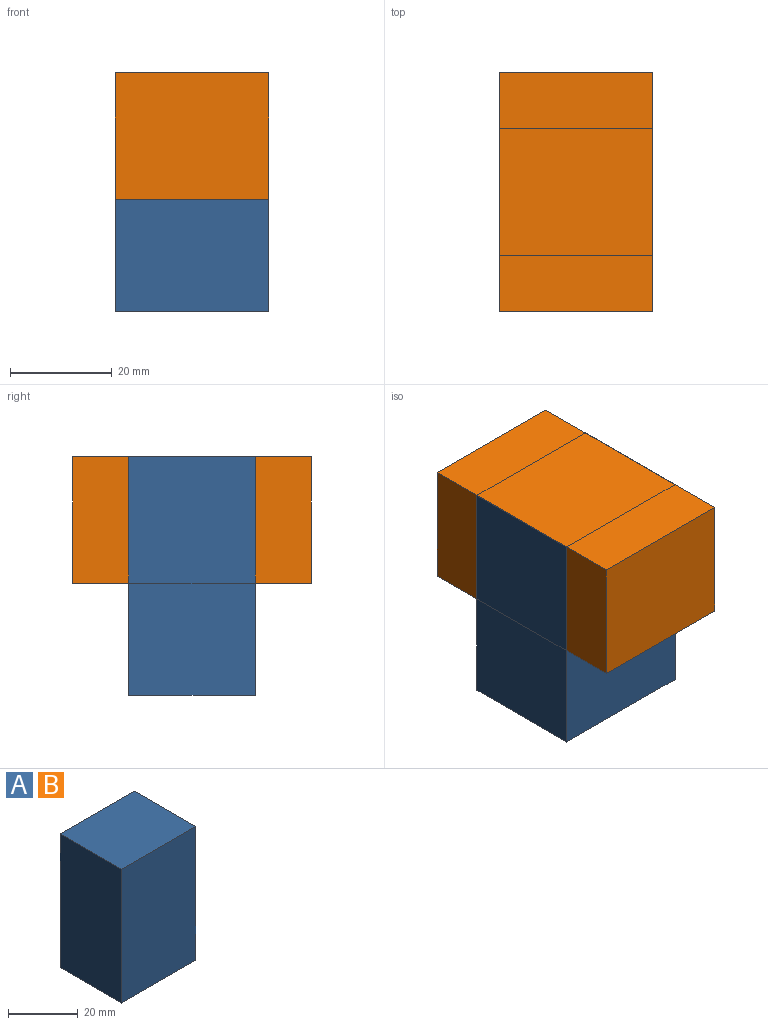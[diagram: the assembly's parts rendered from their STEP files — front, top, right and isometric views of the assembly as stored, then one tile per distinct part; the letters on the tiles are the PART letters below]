
ASSEMBLY  parts=2 mates=1
PART A: 6 faces, bbox 30.2x25x47 mm
  f0: plane 30.18x25mm, normal (0,0,1), area 754.5mm2, adj f1,f3,f4,f5
  f1: plane 47.01x25mm, normal (-1,0,0), area 1175.3mm2, adj f0,f2,f4,f5
  f2: plane 30.18x25mm, normal (0,0,-1), area 754.5mm2, adj f1,f3,f4,f5
  f3: plane 47.01x25mm, normal (1,0,0), area 1175.3mm2, adj f0,f2,f4,f5
  f4: plane 47.01x30.18mm, normal (0,-1,0), area 1418.8mm2, adj f0,f1,f2,f3
  f5: plane 47.01x30.18mm, normal (0,1,0), area 1418.8mm2, adj f0,f1,f2,f3
PART B: same geometry as A
PLACE A at identity
PLACE B rot(axis=(-1,0,0),90deg) t=(0,-36.01,22.01)mm
MATE fastened B.f4 <-> A.f0  axis (0,0,1) through (-45.03,-12.5,47.01)mm
